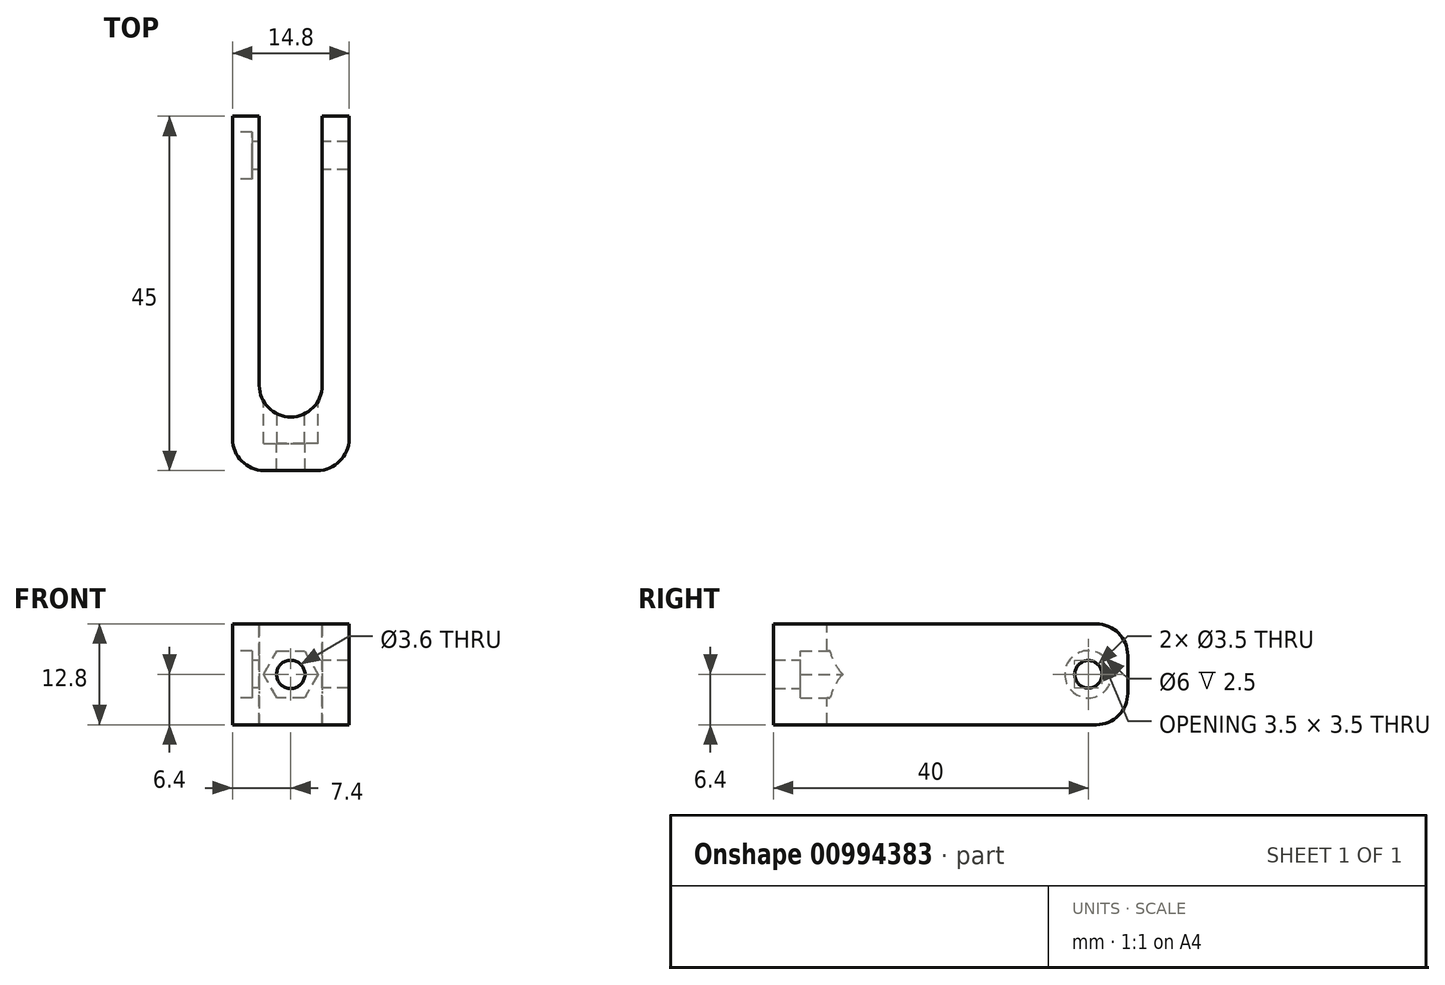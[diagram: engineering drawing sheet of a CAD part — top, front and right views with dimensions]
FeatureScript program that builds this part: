
annotation { "Feature Type Name" : "Feature", "Feature Type Description" : "" }
export const myFeature = defineFeature(function(context is Context, id is Id, definition is map)
    precondition{}
    {
        {
            var Q0;
            Q0=qCreatedBy(makeId("Front.planeOp"),FACE);
            var sketch = newSketch(context, id + "F0", { "sketchPlane" : qUnion([Q0])});
            skLineSegment(sketch, "E0.bottom", {"start": v(0, 0) * mm, "end": v(-14.8, 0) * mm});
            skLineSegment(sketch, "E0.top", {"start": v(0, 12.8) * mm, "end": v(-14.8, 12.8) * mm});
            skLineSegment(sketch, "E0.left", {"start": v(0, 0) * mm, "end": v(0, 12.8) * mm});
            skLineSegment(sketch, "E0.right", {"start": v(-14.8, 0) * mm, "end": v(-14.8, 12.8) * mm});
            skLineSegment(sketch, "E1.bottom", {"start": v(-11.4, 13.4) * mm, "end": v(-3.4, 13.4) * mm});
            skLineSegment(sketch, "E1.top", {"start": v(-11.4, -0.6) * mm, "end": v(-3.4, -0.6) * mm});
            skLineSegment(sketch, "E1.left", {"start": v(-11.4, 13.4) * mm, "end": v(-11.4, -0.6) * mm});
            skLineSegment(sketch, "E1.right", {"start": v(-3.4, 13.4) * mm, "end": v(-3.4, -0.6) * mm});
            skPoint(sketch, "E2", {"position": v(-14.8, 6.4) * mm});
            skPoint(sketch, "E3", {"position": v(-11.4, 6.4) * mm});
            skPoint(sketch, "E4", {"position": v(-7.4, 13.4) * mm});
            skPoint(sketch, "E5", {"position": v(-7.4, 12.8) * mm});
            skCircle(sketch, "E6.cCircle", {"center": v(-7.4, 6.4) * mm, "radius": 3 * mm, "construction": true});
            skLineSegment(sketch, "E6.0", {"start": v(-9.13, 9.4) * mm, "end": v(-5.67, 9.4) * mm});
            skLineSegment(sketch, "E6.1", {"start": v(-5.67, 9.4) * mm, "end": v(-3.94, 6.4) * mm});
            skLineSegment(sketch, "E6.2", {"start": v(-3.94, 6.4) * mm, "end": v(-5.67, 3.4) * mm});
            skLineSegment(sketch, "E6.3", {"start": v(-5.67, 3.4) * mm, "end": v(-9.13, 3.4) * mm});
            skLineSegment(sketch, "E6.4", {"start": v(-9.13, 3.4) * mm, "end": v(-10.86, 6.4) * mm});
            skLineSegment(sketch, "E6.5", {"start": v(-10.86, 6.4) * mm, "end": v(-9.13, 9.4) * mm});
            skPoint(sketch, "E6.0.midPoint", {"position": v(-7.4, 9.4) * mm});
            skCircle(sketch, "E7", {"center": v(-7.4, 6.4) * mm, "radius": 1.8 * mm});
            skSolve(sketch);
        }
        {
            var Q0;
            Q0=makeQuery(id+"F0.imprint","IMPRINT",FACE,{"disambiguationData":[TD([[makeQuery(id+"F0.imprint","IMPRINT",EDGE,{"derivedFrom":sQuery(id+"F0.wireOp",EDGE,"E0.bottom")}),-1.0]])]});
            var Q1;
            Q1=makeQuery(id+"F0.imprint","IMPRINT",FACE,{"disambiguationData":[TD([[makeQuery(id+"F0.imprint","IMPRINT",EDGE,{"derivedFrom":sQuery(id+"F0.wireOp",EDGE,"E6.0")}),1.0]])]});
            var Q2;
            Q2=makeQuery(id+"F0.imprint","IMPRINT",FACE,{"disambiguationData":[TD([[makeQuery(id+"F0.imprint","IMPRINT",EDGE,{"derivedFrom":sQuery(id+"F0.wireOp",EDGE,"E6.0")}),-1.0]])]});
            extrude(context, id + "F1", {"entities" : qUnion([Q0, Q1, Q2]), "depth" : 45 * mm, "offsetDistance" : 25 * mm});
        }
        {
            var Q0;
            Q0=makeQuery(id+"F1.opExtrude","SWEPT_FACE",FACE,{"disambiguationData":[OSD([sQuery(id+"F0.wireOp",EDGE,"E0.right")])]});
            var sketch = newSketch(context, id + "F2", { "sketchPlane" : qUnion([Q0])});
            skCircle(sketch, "E8", {"center": v(5, 6.4) * mm, "radius": 1.75 * mm});
            skLineSegment(sketch, "E9.0", {"start": v(0, 0) * mm, "end": v(0, 12.8) * mm});
            skPoint(sketch, "E10", {"position": v(0, 6.4) * mm});
            skCircle(sketch, "E11", {"center": v(5, 6.4) * mm, "radius": 3 * mm});
            skCircle(sketch, "E12", {"center": v(5, 6.4) * mm, "radius": 7 * mm, "construction": true});
            skSolve(sketch);
        }
        {
            var Q0;
            Q0=makeQuery(id+"F2.imprint","IMPRINT",FACE,{"disambiguationData":[TD([[makeQuery(id+"F2.imprint","IMPRINT",EDGE,{"derivedFrom":sQuery(id+"F2.wireOp",EDGE,"E8")}),1.0]])]});
            extrude(context, id + "F3", {"entities" : qUnion([Q0]), "operationType" : NewBodyOperationType.REMOVE, "oppositeDirection" : true, "depth" : 25 * mm, "offsetDistance" : 25 * mm});
        }
        {
            var Q0;
            Q0=makeQuery(id+"F2.imprint","IMPRINT",FACE,{"disambiguationData":[TD([[makeQuery(id+"F2.imprint","IMPRINT",EDGE,{"derivedFrom":sQuery(id+"F2.wireOp",EDGE,"E8")}),-1.0]])]});
            extrude(context, id + "F4", {"entities" : qUnion([Q0]), "operationType" : NewBodyOperationType.REMOVE, "oppositeDirection" : true, "depth" : 2.5 * mm, "offsetDistance" : 25 * mm});
        }
        {
            var Q0;
            {var subQ5=sQuery(id+"F0.wireOp",EDGE,"E1.bottom");Q0=makeQuery(id+"F0.imprint","IMPRINT",FACE,{"disambiguationData":[TD([[makeQuery(id+"F0.imprint","IMPRINT",EDGE,{"derivedFrom":subQ5}),-1.0]])]});}
            var Q1;
            {var subQ0=sQuery(id+"F0.wireOp",EDGE,"E1.right");var subQ1=sQuery(id+"F0.wireOp",EDGE,"E0.bottom");var subQ2=makeQuery(id+"F0.imprint","INTERSECT",VERTEX,{"derivedFrom":[subQ1,subQ0]});Q1=makeQuery(id+"F0.imprint","IMPRINT",FACE,{"disambiguationData":[TD([[makeQuery(id+"F0.imprint","IMPRINT",EDGE,{"disambiguationData":[TD([[subQ2,-1.0]])],"derivedFrom":subQ1}),-1.0]])]});}
            var Q2;
            {var subQ5=sQuery(id+"F0.wireOp",EDGE,"E1.top");Q2=makeQuery(id+"F0.imprint","IMPRINT",FACE,{"disambiguationData":[TD([[makeQuery(id+"F0.imprint","IMPRINT",EDGE,{"derivedFrom":subQ5}),1.0]])]});}
            var Q3;
            Q3=makeQuery(id+"F0.imprint","IMPRINT",FACE,{"disambiguationData":[TD([[makeQuery(id+"F0.imprint","IMPRINT",EDGE,{"derivedFrom":sQuery(id+"F0.wireOp",EDGE,"E6.0")}),-1.0]])]});
            extrude(context, id + "F5", {"entities" : qUnion([Q0, Q1, Q2, Q3]), "operationType" : NewBodyOperationType.REMOVE, "depth" : (45 - 6.8) * mm, "offsetDistance" : 25 * mm});
        }
        {
            var Q0;
            Q0=makeQuery(id+"F5.boolean.opBoolean","COPY",EDGE,{"derivedFrom":makeQuery(id+"F5.opExtrude","CAP_EDGE",EDGE,{"disambiguationData":[OSD([sQuery(id+"F0.wireOp",EDGE,"E1.right")])],"isStart":false})});
            var Q1;
            Q1=makeQuery(id+"F5.boolean.opBoolean","COPY",EDGE,{"derivedFrom":makeQuery(id+"F5.opExtrude","CAP_EDGE",EDGE,{"disambiguationData":[OSD([sQuery(id+"F0.wireOp",EDGE,"E1.left")])],"isStart":false})});
            var Q2;
            {var subQ0=sQuery(id+"F0.wireOp",EDGE,"E0.left");var subQ1=sQuery(id+"F0.wireOp",EDGE,"E0.top");Q2=makeQuery(id+"F5.boolean.opBoolean","SPLIT",EDGE,{"disambiguationData":[TD([makeQuery(id+"F1.opExtrude","SWEPT_FACE",FACE,{"disambiguationData":[OSD([subQ0])]})])],"derivedFrom":makeQuery(id+"F1.opExtrude","CAP_EDGE",EDGE,{"disambiguationData":[OSD([subQ1])],"isStart":true})});}
            var Q3;
            {var subQ0=sQuery(id+"F0.wireOp",EDGE,"E0.bottom");var subQ1=sQuery(id+"F0.wireOp",EDGE,"E0.left");Q3=makeQuery(id+"F5.boolean.opBoolean","SPLIT",EDGE,{"disambiguationData":[TD([makeQuery(id+"F1.opExtrude","SWEPT_FACE",FACE,{"disambiguationData":[OSD([subQ1])]})])],"derivedFrom":makeQuery(id+"F1.opExtrude","CAP_EDGE",EDGE,{"disambiguationData":[OSD([subQ0])],"isStart":true})});}
            var Q4;
            {var subQ0=sQuery(id+"F0.wireOp",EDGE,"E0.bottom");var subQ1=sQuery(id+"F0.wireOp",EDGE,"E0.right");Q4=makeQuery(id+"F5.boolean.opBoolean","SPLIT",EDGE,{"disambiguationData":[TD([makeQuery(id+"F1.opExtrude","SWEPT_FACE",FACE,{"disambiguationData":[OSD([subQ1])]})])],"derivedFrom":makeQuery(id+"F1.opExtrude","CAP_EDGE",EDGE,{"disambiguationData":[OSD([subQ0])],"isStart":true})});}
            var Q5;
            {var subQ0=sQuery(id+"F0.wireOp",EDGE,"E0.right");var subQ1=sQuery(id+"F0.wireOp",EDGE,"E0.top");Q5=makeQuery(id+"F5.boolean.opBoolean","SPLIT",EDGE,{"disambiguationData":[TD([makeQuery(id+"F1.opExtrude","SWEPT_FACE",FACE,{"disambiguationData":[OSD([subQ0])]})])],"derivedFrom":makeQuery(id+"F1.opExtrude","CAP_EDGE",EDGE,{"disambiguationData":[OSD([subQ1])],"isStart":true})});}
            var Q6;
            Q6=makeQuery(id+"F1.opExtrude","CAP_EDGE",EDGE,{"disambiguationData":[OSD([sQuery(id+"F0.wireOp",EDGE,"E0.right")])],"isStart":false});
            var Q7;
            Q7=makeQuery(id+"F1.opExtrude","CAP_EDGE",EDGE,{"disambiguationData":[OSD([sQuery(id+"F0.wireOp",EDGE,"E0.left")])],"isStart":false});
            fillet(context, id + "F6", {"entities" : qUnion([Q0, Q1, Q2, Q3, Q4, Q5, Q6, Q7]), "tangentPropagation" : true, "radius" : 4 * mm, "defaultsChanged" : false, "vertexSettings" : [], "allowEdgeOverflow" : false});
        }
        {
            var Q0;
            Q0=makeQuery(id+"F0.imprint","IMPRINT",FACE,{"disambiguationData":[TD([[makeQuery(id+"F0.imprint","IMPRINT",EDGE,{"derivedFrom":sQuery(id+"F0.wireOp",EDGE,"E6.0")}),-1.0]])]});
            extrude(context, id + "F7", {"entities" : qUnion([Q0]), "operationType" : NewBodyOperationType.REMOVE, "depth" : (45 - 3.4) * mm, "offsetDistance" : 25 * mm});
        }
    });
